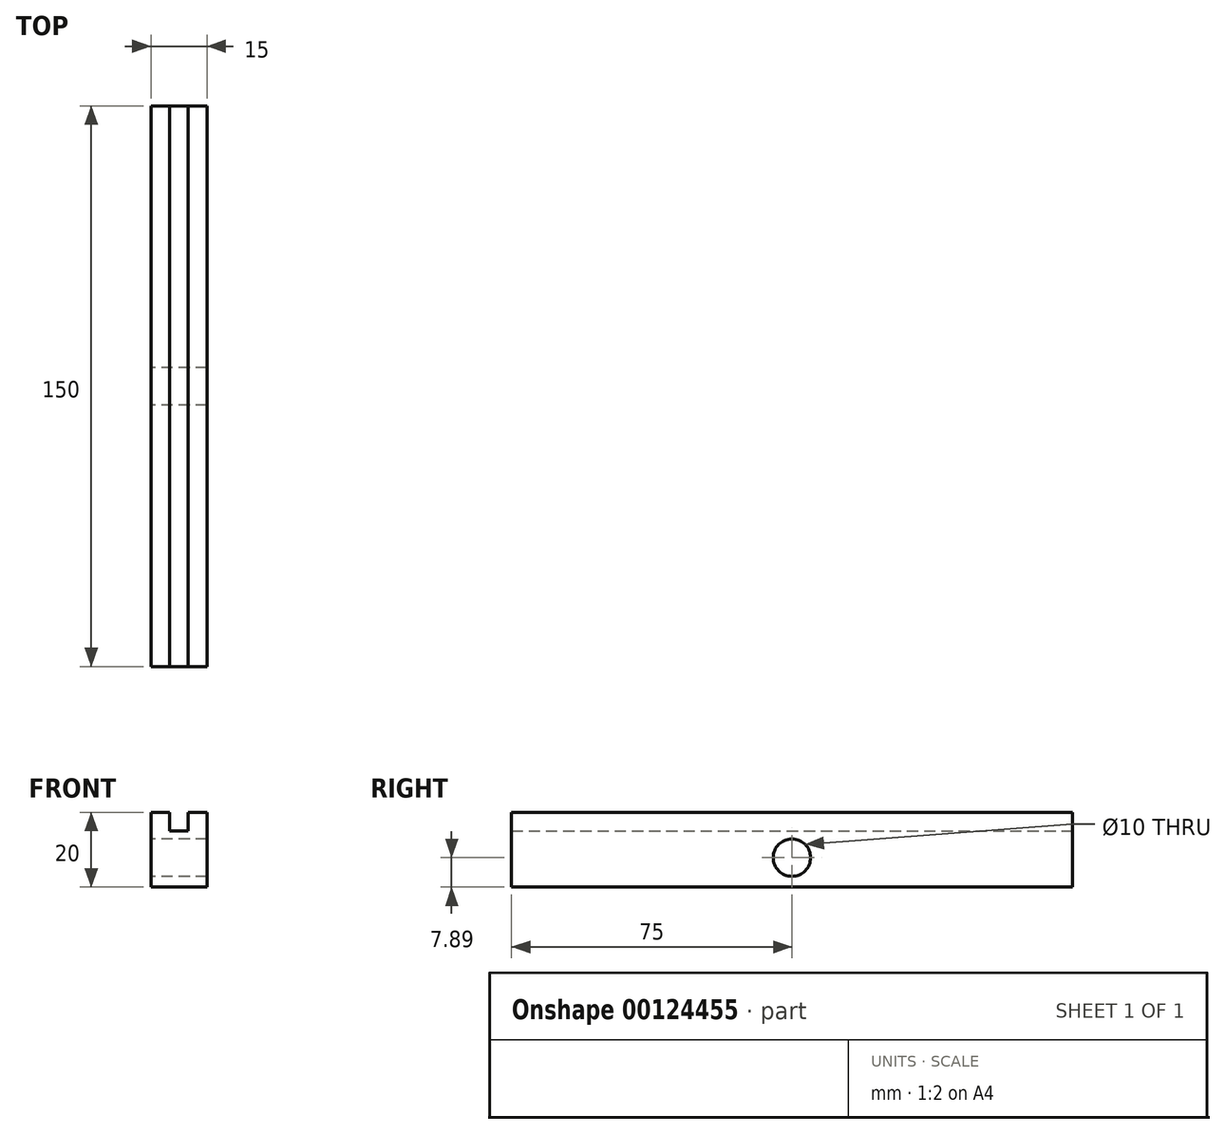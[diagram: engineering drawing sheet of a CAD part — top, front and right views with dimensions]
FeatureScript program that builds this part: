
annotation { "Feature Type Name" : "Feature", "Feature Type Description" : "" }
export const myFeature = defineFeature(function(context is Context, id is Id, definition is map)
    precondition{}
    {
        {
            var Q0;
            Q0=qCreatedBy(makeId("Front.planeOp"),FACE);
            var sketch = newSketch(context, id + "F0", { "sketchPlane" : qUnion([Q0])});
            skLineSegment(sketch, "E0", {"start": v(-19.46, 12.11) * mm, "end": v(-19.46, -7.89) * mm});
            skLineSegment(sketch, "E1", {"start": v(-19.46, -7.89) * mm, "end": v(-4.46, -7.89) * mm});
            skLineSegment(sketch, "E2", {"start": v(-4.46, -7.89) * mm, "end": v(-4.46, 12.11) * mm});
            skLineSegment(sketch, "E3", {"start": v(-19.46, 12.11) * mm, "end": v(-14.46, 12.11) * mm});
            skLineSegment(sketch, "E4", {"start": v(-14.46, 12.11) * mm, "end": v(-14.46, 7.11) * mm});
            skLineSegment(sketch, "E5", {"start": v(-14.46, 7.11) * mm, "end": v(-9.46, 7.11) * mm});
            skLineSegment(sketch, "E6", {"start": v(-9.46, 7.11) * mm, "end": v(-9.46, 12.11) * mm});
            skLineSegment(sketch, "E7", {"start": v(-4.46, 12.11) * mm, "end": v(-9.46, 12.11) * mm});
            skSolve(sketch);
        }
        {
            var Q0;
            Q0=makeQuery(id+"F0.imprint","IMPRINT",FACE,{"disambiguationData":[TD([[makeQuery(id+"F0.imprint","IMPRINT",EDGE,{"derivedFrom":sQuery(id+"F0.wireOp",EDGE,"E0")}),1.0]])]});
            extrude(context, id + "F1", {"entities" : qUnion([Q0]), "endBound" : BoundingType.SYMMETRIC, "depth" : 150 * mm});
        }
        {
            var Q0;
            Q0=makeQuery(id+"F1.opExtrude","SWEPT_FACE",FACE,{"disambiguationData":[OSD([sQuery(id+"F0.wireOp",EDGE,"E0")])]});
            var sketch = newSketch(context, id + "F2", { "sketchPlane" : qUnion([Q0])});
            skCircle(sketch, "E8", {"center": v(0, 0) * mm, "radius": 5 * mm});
            skSolve(sketch);
        }
        {
            var Q0;
            Q0=sQuery(id+"F2.wireOp",VERTEX,"E8.center");
            var Q1;
            Q1=makeQuery(id+"F1.opExtrude","SWEPT_BODY",BODY,{"disambiguationData":[OSD([sQuery(id+"F0.wireOp",EDGE,"E0"),sQuery(id+"F0.wireOp",EDGE,"E1"),sQuery(id+"F0.wireOp",EDGE,"E2"),sQuery(id+"F0.wireOp",EDGE,"E3"),sQuery(id+"F0.wireOp",EDGE,"E4"),sQuery(id+"F0.wireOp",EDGE,"E5"),sQuery(id+"F0.wireOp",EDGE,"E6"),sQuery(id+"F0.wireOp",EDGE,"E7")])]});
            hole(context, id + "F3", {"style" : HoleStyle.SIMPLE, "endStyle" : HoleEndStyle.THROUGH, "holeDiameter" : 10 * mm, "locations" : qUnion([Q0]), "scope" : qUnion([Q1]), "isTappedThrough" : true});
        }
    });
